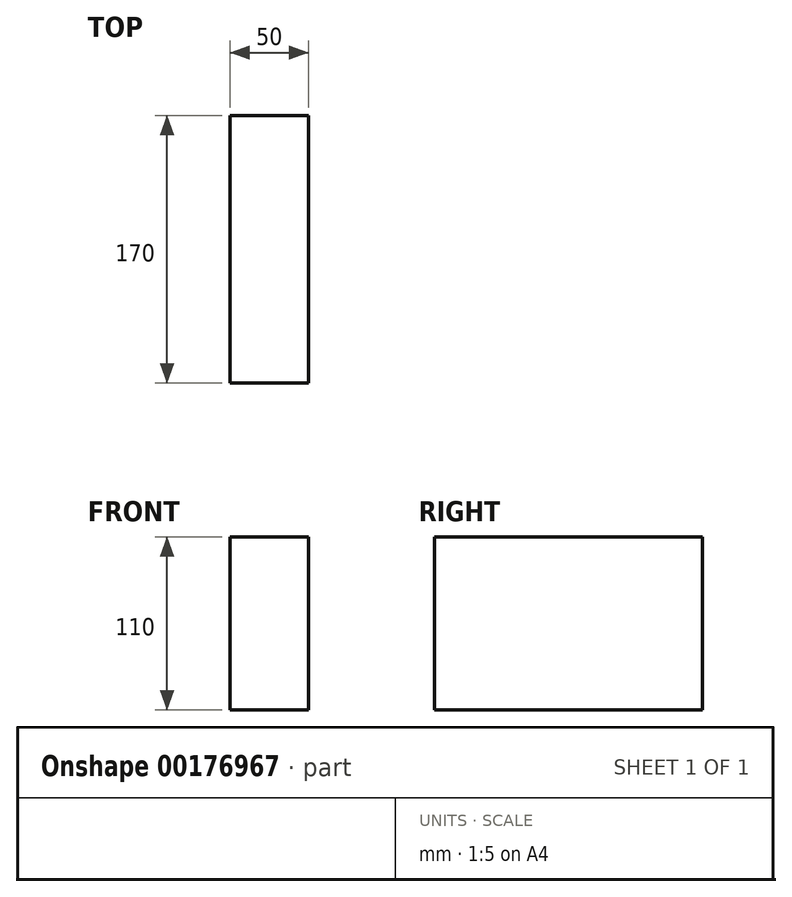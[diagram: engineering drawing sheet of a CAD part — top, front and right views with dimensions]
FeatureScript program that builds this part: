
annotation { "Feature Type Name" : "Feature", "Feature Type Description" : "" }
export const myFeature = defineFeature(function(context is Context, id is Id, definition is map)
    precondition{}
    {
        {
            assignVariable(context, id + "F0", {"name" : "probeHeight", "anyValue" : 110});
        }
        {
            var Q0;
            Q0=qCreatedBy(makeId("Top.planeOp"),FACE);
            var sketch = newSketch(context, id + "F1", { "sketchPlane" : qUnion([Q0])});
            skLineSegment(sketch, "E0.bottom", {"start": v(-25, 85) * mm, "end": v(25, 85) * mm});
            skLineSegment(sketch, "E0.top", {"start": v(-25, -85) * mm, "end": v(25, -85) * mm});
            skLineSegment(sketch, "E0.left", {"start": v(-25, 85) * mm, "end": v(-25, -85) * mm});
            skLineSegment(sketch, "E0.right", {"start": v(25, 85) * mm, "end": v(25, -85) * mm});
            skPoint(sketch, "E0.middle", {"position": v(0, 0) * mm});
            skSolve(sketch);
        }
        {
            var Q0;
            Q0=qSketchRegion(id+"F1",true);
            extrude(context, id + "F2", {"entities" : qUnion([Q0]), "depth" : (getVariable(context, 'probeHeight')) * mm});
        }
    });
